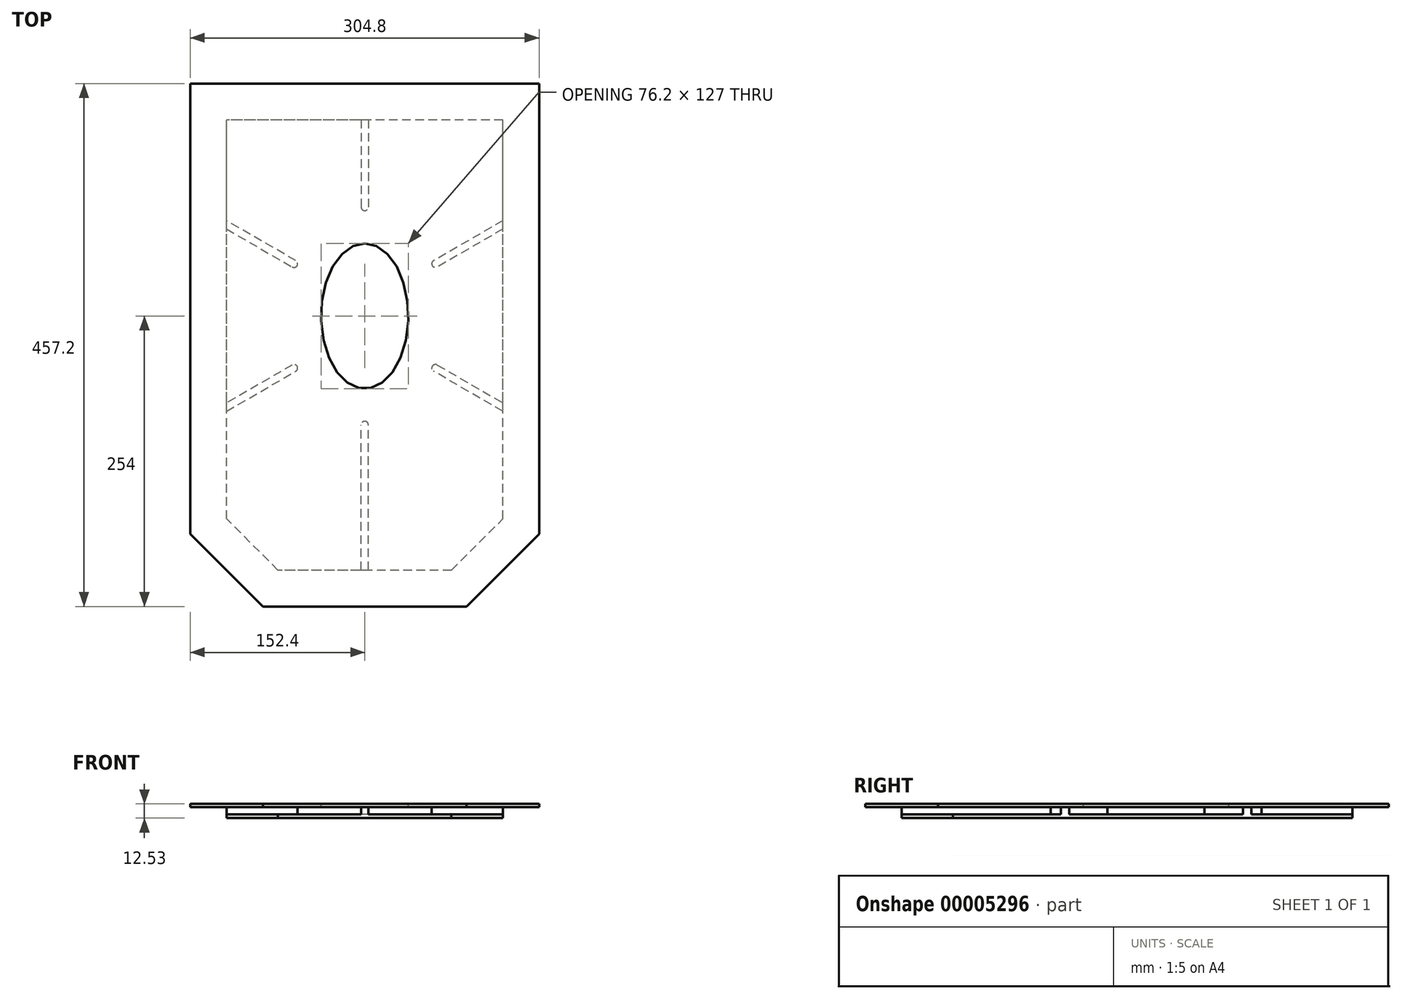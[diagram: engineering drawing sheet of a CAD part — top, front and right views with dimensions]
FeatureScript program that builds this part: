
annotation { "Feature Type Name" : "Feature", "Feature Type Description" : "" }
export const myFeature = defineFeature(function(context is Context, id is Id, definition is map)
    precondition{}
    {
        {
            var Q0;
            Q0=qCreatedBy(makeId("Top.planeOp"),FACE);
            var sketch = newSketch(context, id + "F0", { "sketchPlane" : qUnion([Q0])});
            skLineSegment(sketch, "E0.rect.bottom", {"start": v(152.4, -228.6) * mm, "end": v(-152.4, -228.6) * mm});
            skLineSegment(sketch, "E0.rect.top", {"start": v(152.4, 228.6) * mm, "end": v(-152.4, 228.6) * mm});
            skLineSegment(sketch, "E0.rect.left", {"start": v(152.4, -228.6) * mm, "end": v(152.4, 228.6) * mm});
            skLineSegment(sketch, "E0.rect.right", {"start": v(-152.4, -228.6) * mm, "end": v(-152.4, 228.6) * mm});
            skPoint(sketch, "E0.rect.middle", {"position": v(0, 0) * mm});
            skSolve(sketch);
        }
        {
            var Q0;
            Q0=makeQuery(id+"F0.imprint","IMPRINT",FACE,{"disambiguationData":[TD([[makeQuery(id+"F0.imprint","IMPRINT",EDGE,{"derivedFrom":sQuery(id+"F0.wireOp",EDGE,"E0.rect.bottom")}),-1.0]])]});
            extrude(context, id + "F1", {"entities" : qUnion([Q0]), "depth" : 3 * mm});
        }
        {
            var Q0;
            Q0=makeQuery(id+"F1.opExtrude","SWEPT_EDGE",EDGE,{"disambiguationData":[OSD([sQuery(id+"F0.wireOp",EDGE,"E0.rect.bottom"),sQuery(id+"F0.wireOp",EDGE,"E0.rect.left")])]});
            var Q1;
            Q1=makeQuery(id+"F1.opExtrude","SWEPT_EDGE",EDGE,{"disambiguationData":[OSD([sQuery(id+"F0.wireOp",EDGE,"E0.rect.bottom"),sQuery(id+"F0.wireOp",EDGE,"E0.rect.right")])]});
            chamfer(context, id + "F2", {"entities" : qUnion([Q0, Q1]), "width" : 63.5 * mm, "tangentPropagation" : true});
        }
        {
            var Q0;
            Q0=makeQuery(id+"F1.opExtrude","CAP_FACE",FACE,{"disambiguationData":[OSD([sQuery(id+"F0.wireOp",EDGE,"E0.rect.bottom"),sQuery(id+"F0.wireOp",EDGE,"E0.rect.top"),sQuery(id+"F0.wireOp",EDGE,"E0.rect.left"),sQuery(id+"F0.wireOp",EDGE,"E0.rect.right")])],"isStart":false});
            var sketch = newSketch(context, id + "F3", { "sketchPlane" : qUnion([Q0])});
            skEllipse(sketch, "E1", {"center": v(0, 25.4) * mm, "majorRadius": 63.5 * mm, "minorRadius": 38.1 * mm, "majorAxis": v(0, 1)});
            skPoint(sketch, "E2", {"position": v(0, -38.1) * mm});
            skSolve(sketch);
        }
        {
            var Q0;
            Q0=makeQuery(id+"F3.imprint","IMPRINT",FACE,{"disambiguationData":[TD([[makeQuery(id+"F3.imprint","IMPRINT",EDGE,{"derivedFrom":sQuery(id+"F3.wireOp",EDGE,"E1")}),1.0]])]});
            extrude(context, id + "F4", {"entities" : qUnion([Q0]), "operationType" : NewBodyOperationType.REMOVE, "endBound" : BoundingType.UP_TO_NEXT, "oppositeDirection" : true, "depth" : 25.4 * mm});
        }
        {
            var Q0;
            Q0=makeQuery(id+"F1.opExtrude","CAP_FACE",FACE,{"disambiguationData":[OSD([sQuery(id+"F0.wireOp",EDGE,"E0.rect.bottom"),sQuery(id+"F0.wireOp",EDGE,"E0.rect.top"),sQuery(id+"F0.wireOp",EDGE,"E0.rect.left"),sQuery(id+"F0.wireOp",EDGE,"E0.rect.right")])],"isStart":true});
            var sketch = newSketch(context, id + "F5", { "sketchPlane" : qUnion([Q0])});
            skFitSpline(sketch, "E3.0", {"points": [v(0, -88.9) * mm, v(1000, 76.2) * mm, v(-88.9, 333.33) * mm, v(76.2, 38.1) * mm, v(333.33, 0) * mm, v(38.1, 1000) * mm, v(-76.2, 38.1) * mm, v(0, -88.9) * mm], "construction": true});
            skFitSpline(sketch, "E4.0", {"points": [v(-0.71, -120.65) * mm, v(0, -120.65) * mm, v(0.71, -120.65) * mm, v(1.67, -120.63) * mm, v(2.88, -120.58) * mm, v(4.36, -120.48) * mm, v(6.35, -120.3) * mm, v(8.88, -119.95) * mm, v(11.97, -119.36) * mm, v(15.1, -118.57) * mm, v(19.3, -117.24) * mm, v(24.57, -115.06) * mm, v(30.78, -111.58) * mm, v(36.77, -107.26) * mm, v(42.44, -102.1) * mm, v(49.49, -94.18) * mm, v(55.65, -84.72) * mm, v(60.74, -73.85) * mm, v(63.96, -65.05) * mm, v(66.55, -55.7) * mm, v(68.44, -45.87) * mm, v(69.6, -35.72) * mm, v(69.98, -25.4) * mm, v(69.6, -15.08) * mm, v(68.44, -4.93) * mm, v(66.55, 4.9) * mm, v(63.96, 14.25) * mm, v(60.74, 23.05) * mm, v(55.65, 33.92) * mm, v(49.49, 43.38) * mm, v(42.44, 51.3) * mm, v(36.77, 56.46) * mm, v(30.78, 60.78) * mm, v(24.57, 64.26) * mm, v(19.3, 66.44) * mm, v(15.1, 67.77) * mm, v(11.97, 68.56) * mm, v(8.88, 69.15) * mm, v(6.35, 69.5) * mm, v(4.36, 69.68) * mm, v(2.88, 69.78) * mm, v(1.67, 69.83) * mm, v(0.71, 69.85) * mm, v(0, 69.85) * mm, v(-0.71, 69.85) * mm, v(-1.67, 69.83) * mm, v(-2.88, 69.78) * mm, v(-4.36, 69.68) * mm, v(-6.35, 69.5) * mm, v(-8.88, 69.15) * mm, v(-11.97, 68.56) * mm, v(-15.1, 67.77) * mm, v(-19.3, 66.44) * mm, v(-24.57, 64.26) * mm, v(-30.78, 60.78) * mm, v(-36.77, 56.46) * mm, v(-42.44, 51.3) * mm, v(-49.49, 43.38) * mm, v(-55.65, 33.92) * mm, v(-60.74, 23.05) * mm, v(-63.96, 14.25) * mm, v(-66.55, 4.9) * mm, v(-68.44, -4.93) * mm, v(-69.6, -15.08) * mm, v(-69.98, -25.4) * mm, v(-69.6, -35.72) * mm, v(-68.44, -45.87) * mm, v(-66.55, -55.7) * mm, v(-63.96, -65.05) * mm, v(-60.74, -73.85) * mm, v(-55.65, -84.72) * mm, v(-49.49, -94.18) * mm, v(-42.44, -102.1) * mm, v(-36.77, -107.26) * mm, v(-30.78, -111.58) * mm, v(-24.57, -115.06) * mm, v(-19.3, -117.24) * mm, v(-15.1, -118.57) * mm, v(-11.97, -119.36) * mm, v(-8.88, -119.95) * mm, v(-6.35, -120.3) * mm, v(-4.36, -120.48) * mm, v(-2.88, -120.58) * mm, v(-1.67, -120.63) * mm, v(-0.71, -120.65) * mm, v(0, -120.65) * mm, v(0.71, -120.65) * mm, v(-0.71, -120.65) * mm], "construction": true});
            skLineSegment(sketch, "E5", {"start": v(3.17, -196.85) * mm, "end": v(3.17, -120.65) * mm});
            skLineSegment(sketch, "E6", {"start": v(-3.17, -196.85) * mm, "end": v(-3.18, -120.65) * mm});
            skLineSegment(sketch, "E7", {"start": v(3.17, -228.6) * mm, "end": v(-3.17, -228.6) * mm});
            skPoint(sketch, "E8", {"position": v(0, -228.6) * mm});
            skArc(sketch, "E9", {"start": v(3.18, -120.65) * mm, "mid": v(0, -117.47) * mm, "end": v(-3.18, -120.65) * mm});
            skLineSegment(sketch, "E10", {"start": v(3.17, 196.85) * mm, "end": v(3.17, 69.85) * mm});
            skLineSegment(sketch, "E11", {"start": v(-3.18, 196.85) * mm, "end": v(-3.18, 69.85) * mm});
            skArc(sketch, "E12", {"start": v(3.18, 69.85) * mm, "mid": v(0, 66.67) * mm, "end": v(-3.18, 69.85) * mm});
            skLineSegment(sketch, "E13", {"start": v(120.65, -101.34) * mm, "end": v(63.33, -68.24) * mm});
            skLineSegment(sketch, "E14", {"start": v(120.65, -108.67) * mm, "end": v(60.15, -73.74) * mm});
            skArc(sketch, "E15", {"start": v(63.33, -68.24) * mm, "mid": v(58.99, -69.4) * mm, "end": v(60.15, -73.74) * mm});
            skLineSegment(sketch, "E16", {"start": v(63.33, 17.44) * mm, "end": v(120.65, 50.54) * mm});
            skLineSegment(sketch, "E17", {"start": v(152.4, 68.87) * mm, "end": v(152.4, 76.2) * mm});
            skLineSegment(sketch, "E18", {"start": v(120.65, 57.87) * mm, "end": v(60.15, 22.94) * mm});
            skArc(sketch, "E19", {"start": v(60.15, 22.94) * mm, "mid": v(58.99, 18.6) * mm, "end": v(63.33, 17.44) * mm});
            skLineSegment(sketch, "E20", {"start": v(-60.15, -73.74) * mm, "end": v(-120.65, -108.67) * mm});
            skLineSegment(sketch, "E21", {"start": v(-120.65, -101.34) * mm, "end": v(-63.33, -68.24) * mm});
            skLineSegment(sketch, "E22", {"start": v(-63.33, 17.44) * mm, "end": v(-120.65, 50.54) * mm});
            skLineSegment(sketch, "E23", {"start": v(-120.65, 57.87) * mm, "end": v(-60.15, 22.94) * mm});
            skArc(sketch, "E24", {"start": v(-60.15, 22.94) * mm, "mid": v(-58.99, 18.6) * mm, "end": v(-63.33, 17.44) * mm});
            skArc(sketch, "E25", {"start": v(-60.15, -73.74) * mm, "mid": v(-58.99, -69.4) * mm, "end": v(-63.33, -68.24) * mm});
            skLineSegment(sketch, "E26.1", {"start": v(120.65, 57.87) * mm, "end": v(120.65, 50.54) * mm});
            skLineSegment(sketch, "E26.2", {"start": v(3.17, -196.85) * mm, "end": v(-3.17, -196.85) * mm});
            skLineSegment(sketch, "E26.3", {"start": v(-120.65, 57.87) * mm, "end": v(-120.65, 50.54) * mm});
            skLineSegment(sketch, "E26.5", {"start": v(3.18, 196.85) * mm, "end": v(-3.18, 196.85) * mm});
            skPoint(sketch, "E27.end.orphan", {"position": v(-152.4, 76.2) * mm});
            skLineSegment(sketch, "E28.trimOffspring", {"start": v(-120.65, -101.34) * mm, "end": v(-120.65, -108.67) * mm});
            skPoint(sketch, "E29.start.orphan", {"position": v(-152.4, -127) * mm});
            skPoint(sketch, "E30.end.orphan", {"position": v(152.4, -127) * mm});
            skLineSegment(sketch, "E31.trimOffspring", {"start": v(120.65, -101.34) * mm, "end": v(120.65, -108.67) * mm});
            skSolve(sketch);
        }
        {
            var Q0;
            {Q0=qUnion([makeQuery(id+"F5.imprint","IMPRINT",FACE,{"disambiguationData":[TD([[makeQuery(id+"F5.imprint","IMPRINT",EDGE,{"derivedFrom":sQuery(id+"F5.wireOp",EDGE,"E5")}),1.0]])]}),makeQuery(id+"F5.imprint","IMPRINT",FACE,{"disambiguationData":[TD([[makeQuery(id+"F5.imprint","IMPRINT",EDGE,{"derivedFrom":sQuery(id+"F5.wireOp",EDGE,"E10")}),-1.0]])]}),makeQuery(id+"F5.imprint","IMPRINT",FACE,{"disambiguationData":[TD([[makeQuery(id+"F5.imprint","IMPRINT",EDGE,{"derivedFrom":sQuery(id+"F5.wireOp",EDGE,"E13")}),1.0]])]}),makeQuery(id+"F5.imprint","IMPRINT",FACE,{"disambiguationData":[TD([[makeQuery(id+"F5.imprint","IMPRINT",EDGE,{"derivedFrom":sQuery(id+"F5.wireOp",EDGE,"E16")}),1.0]])]}),makeQuery(id+"F5.imprint","IMPRINT",FACE,{"disambiguationData":[TD([[makeQuery(id+"F5.imprint","IMPRINT",EDGE,{"derivedFrom":sQuery(id+"F5.wireOp",EDGE,"E20")}),-1.0]])]}),makeQuery(id+"F5.imprint","IMPRINT",FACE,{"disambiguationData":[TD([[makeQuery(id+"F5.imprint","IMPRINT",EDGE,{"derivedFrom":sQuery(id+"F5.wireOp",EDGE,"E22")}),-1.0]])]})]);}
            extrude(context, id + "F6", {"entities" : qUnion([Q0]), "operationType" : NewBodyOperationType.ADD, "depth" : 6.35 * mm});
        }
        {
            var Q0;
            Q0=makeQuery(id+"F6.opExtrude","CAP_FACE",FACE,{"disambiguationData":[OSD([sQuery(id+"F5.wireOp",EDGE,"E10"),sQuery(id+"F5.wireOp",EDGE,"E11"),sQuery(id+"F5.wireOp",EDGE,"E12"),sQuery(id+"F5.wireOp",EDGE,"E26.5")])],"isStart":false});
            var sketch = newSketch(context, id + "F7", { "sketchPlane" : qUnion([Q0])});
            skLineSegment(sketch, "E32.0.0", {"start": v(-152.4, 165.1) * mm, "end": v(-152.4, -228.6) * mm, "construction": true});
            skLineSegment(sketch, "E32.0.1", {"start": v(-88.9, 228.6) * mm, "end": v(-152.4, 165.1) * mm, "construction": true});
            skLineSegment(sketch, "E32.0.2", {"start": v(88.9, 228.6) * mm, "end": v(-88.9, 228.6) * mm, "construction": true});
            skLineSegment(sketch, "E32.0.3", {"start": v(88.9, 228.6) * mm, "end": v(152.4, 165.1) * mm, "construction": true});
            skLineSegment(sketch, "E32.0.4", {"start": v(152.4, 165.1) * mm, "end": v(152.4, -228.6) * mm, "construction": true});
            skLineSegment(sketch, "E32.0.5", {"start": v(152.4, -228.6) * mm, "end": v(-152.4, -228.6) * mm, "construction": true});
            skLineSegment(sketch, "E33.0", {"start": v(-120.65, 151.95) * mm, "end": v(-120.65, -196.85) * mm});
            skLineSegment(sketch, "E33.1", {"start": v(-75.75, 196.85) * mm, "end": v(-120.65, 151.95) * mm});
            skLineSegment(sketch, "E33.2", {"start": v(75.75, 196.85) * mm, "end": v(-75.75, 196.85) * mm});
            skLineSegment(sketch, "E33.3", {"start": v(75.75, 196.85) * mm, "end": v(120.65, 151.95) * mm});
            skLineSegment(sketch, "E33.4", {"start": v(120.65, 151.95) * mm, "end": v(120.65, -196.85) * mm});
            skLineSegment(sketch, "E33.5", {"start": v(120.65, -196.85) * mm, "end": v(-120.65, -196.85) * mm});
            skSolve(sketch);
        }
        {
            var Q0;
            Q0 = qSketchRegion(id + "F7", true);
            extrude(context, id + "F8", {"entities" : qUnion([Q0]), "operationType" : NewBodyOperationType.ADD, "depth" : 3.17 * mm});
        }
        {
            var Q0;
            Q0=qCreatedBy(makeId("Right.planeOp"),FACE);
            var sketch = newSketch(context, id + "F9", { "sketchPlane" : qUnion([Q0])});
            skArc(sketch, "E34", {"start": v(228.6, 3) * mm, "mid": v(247.15, -20.38) * mm, "end": v(220.16, -33.13) * mm});
            skArc(sketch, "E35", {"start": v(220.16, -33.13) * mm, "mid": v(206.52, -23.28) * mm, "end": v(196.85, -9.52) * mm});
            skSolve(sketch);
        }
        {
            var Q0;
            Q0 = qSketchRegion(id + "F9", true);
            var Q1;
            Q1=sQuery(id+"F9.wireOp",EDGE,"E35");
            var Q2;
            Q2=sQuery(id+"F9.wireOp",EDGE,"E34");
            var Q3;
            Q3=makeQuery(id+"F1.opExtrude","CAP_EDGE",EDGE,{"disambiguationData":[OSD([sQuery(id+"F0.wireOp",EDGE,"E0.rect.top")])],"isStart":false});
            var Q4;
            Q4=makeQuery(id+"F1.opExtrude","CAP_EDGE",EDGE,{"disambiguationData":[OSD([sQuery(id+"F0.wireOp",EDGE,"E0.rect.right")])],"isStart":false});
            var Q5;
            {var subQ0=sQuery(id+"F0.wireOp",EDGE,"E0.rect.bottom");var subQ1=sQuery(id+"F0.wireOp",EDGE,"E0.rect.right");Q5=makeQuery(id+"F2.opChamfer","BLEND_EDGE",EDGE,{"blendedFrom":[makeQuery(id+"F1.opExtrude","SWEPT_EDGE",EDGE,{"disambiguationData":[OSD([subQ0,subQ1])]}),makeQuery(id+"F1.opExtrude","CAP_FACE",FACE,{"disambiguationData":[OSD([subQ0,sQuery(id+"F0.wireOp",EDGE,"E0.rect.top"),sQuery(id+"F0.wireOp",EDGE,"E0.rect.left"),subQ1])],"isStart":false})],"blendedInto":[makeQuery(id+"F1.opExtrude","CAP_FACE",FACE,{"disambiguationData":[OSD([subQ0,sQuery(id+"F0.wireOp",EDGE,"E0.rect.top"),sQuery(id+"F0.wireOp",EDGE,"E0.rect.left"),subQ1])],"isStart":false})]});}
            var Q6;
            Q6=makeQuery(id+"F1.opExtrude","CAP_EDGE",EDGE,{"disambiguationData":[OSD([sQuery(id+"F0.wireOp",EDGE,"E0.rect.bottom")])],"isStart":false});
            var Q7;
            {var subQ0=sQuery(id+"F0.wireOp",EDGE,"E0.rect.bottom");var subQ1=sQuery(id+"F0.wireOp",EDGE,"E0.rect.left");Q7=makeQuery(id+"F2.opChamfer","BLEND_EDGE",EDGE,{"blendedFrom":[makeQuery(id+"F1.opExtrude","SWEPT_EDGE",EDGE,{"disambiguationData":[OSD([subQ0,subQ1])]}),makeQuery(id+"F1.opExtrude","CAP_FACE",FACE,{"disambiguationData":[OSD([subQ0,sQuery(id+"F0.wireOp",EDGE,"E0.rect.top"),subQ1,sQuery(id+"F0.wireOp",EDGE,"E0.rect.right")])],"isStart":false})],"blendedInto":[makeQuery(id+"F1.opExtrude","CAP_FACE",FACE,{"disambiguationData":[OSD([subQ0,sQuery(id+"F0.wireOp",EDGE,"E0.rect.top"),subQ1,sQuery(id+"F0.wireOp",EDGE,"E0.rect.right")])],"isStart":false})]});}
            var Q8;
            Q8=makeQuery(id+"F1.opExtrude","CAP_EDGE",EDGE,{"disambiguationData":[OSD([sQuery(id+"F0.wireOp",EDGE,"E0.rect.left")])],"isStart":false});
            sweep(context, id + "F10", {"bodyType" : ToolBodyType.SURFACE, "profiles" : qUnion([Q0]), "surfaceProfiles" : qUnion([Q1, Q2]), "path" : qUnion([Q3, Q4, Q5, Q6, Q7, Q8])});
        }
    });
